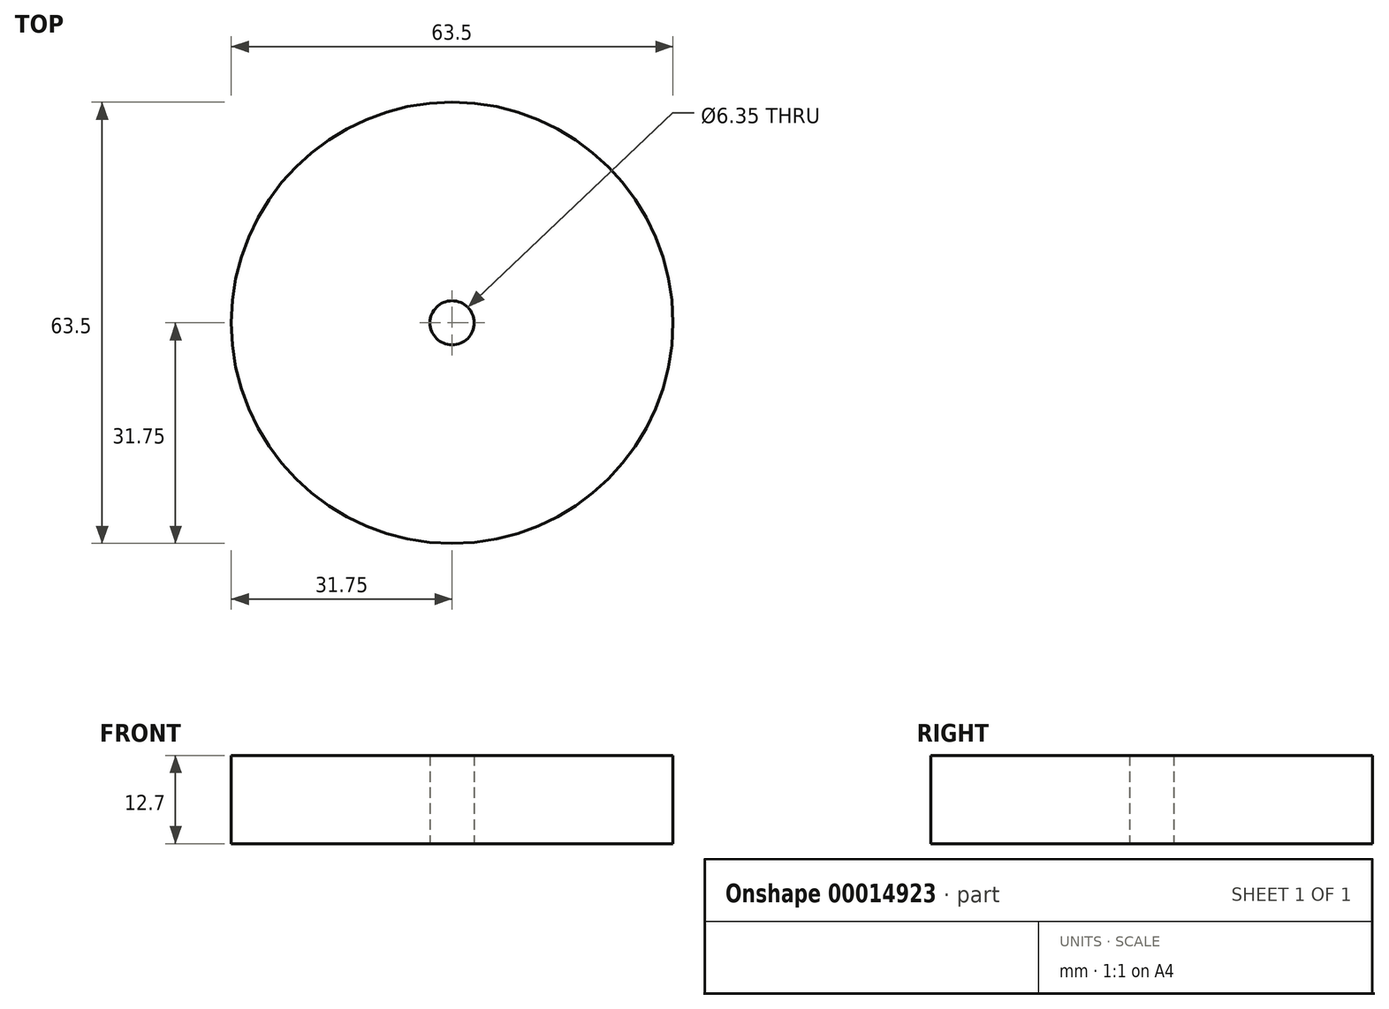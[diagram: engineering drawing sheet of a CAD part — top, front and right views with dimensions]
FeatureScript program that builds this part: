
annotation { "Feature Type Name" : "Feature", "Feature Type Description" : "" }
export const myFeature = defineFeature(function(context is Context, id is Id, definition is map)
    precondition{}
    {
        {
            var Q0;
            Q0=qCreatedBy(makeId("Top.planeOp"),FACE);
            var sketch = newSketch(context, id + "F0", { "sketchPlane" : qUnion([Q0])});
            skCircle(sketch, "E0", {"center": v(0, 0) * mm, "radius": 31.75 * mm});
            skCircle(sketch, "E1", {"center": v(0, 0) * mm, "radius": 3.18 * mm});
            skSolve(sketch);
        }
        {
            var Q0;
            Q0=makeQuery(id+"F0.imprint","IMPRINT",FACE,{"disambiguationData":[TD([[makeQuery(id+"F0.imprint","IMPRINT",EDGE,{"derivedFrom":sQuery(id+"F0.wireOp",EDGE,"E0")}),1.0]])]});
            extrude(context, id + "F1", {"entities" : qUnion([Q0]), "depth" : 12.7 * mm});
        }
    });
